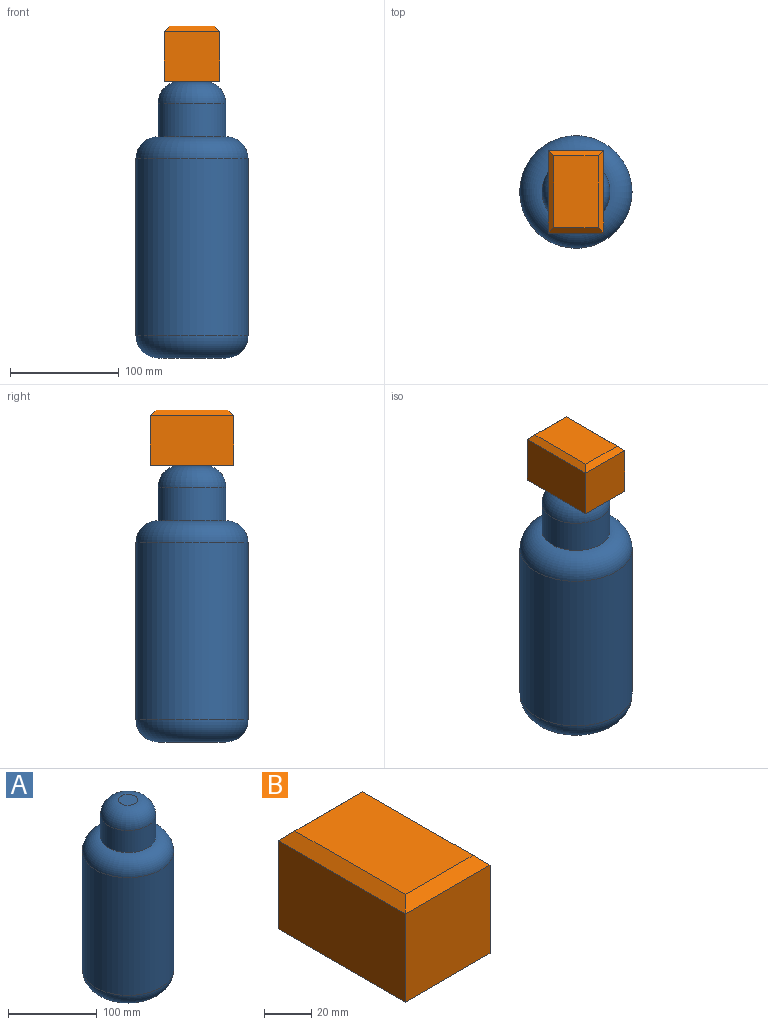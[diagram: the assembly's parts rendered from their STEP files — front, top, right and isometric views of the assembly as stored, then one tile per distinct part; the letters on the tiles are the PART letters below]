
ASSEMBLY  parts=2 mates=1
PART A: 7 faces, bbox 111.5x111.5x254 mm
  f0: cylinder r=51.5mm len=162.56mm, axis (0,0,-1), area 52597mm2, adj f2,f3
  f1: plane 62.35x62.35mm, normal (0,0,-1), area 3053.3mm2, adj f2
  f2: torus R=31.18mm, axis (0,0,1), area 8846.6mm2, adj f0,f1
  f3: torus R=31.18mm, axis (0,0,1), area 8846.6mm2, adj f0,f4
  f4: cylinder r=31.18mm len=62.35mm, axis (0,0,-1), area 5970.4mm2, adj f3,f6
  f5: plane 21.71x21.71mm, normal (0,0,1), area 370.2mm2, adj f6
  f6: torus R=10.86mm, axis (0,0,1), area 4771.4mm2, adj f4,f5
PART B: 10 faces, bbox 50.8x76.2x50.8 mm
  f0: plane 76.2x45.72mm, normal (1,0,0), area 3483.9mm2, adj f1,f3,f5,f7
  f1: plane 50.8x45.72mm, normal (0,1,0), area 2322.6mm2, adj f0,f2,f5,f9
  f2: plane 76.2x45.72mm, normal (-1,0,0), area 3483.9mm2, adj f1,f3,f5,f8
  f3: plane 50.8x45.72mm, normal (0,-1,0), area 2322.6mm2, adj f0,f2,f5,f6
  f4: plane 66.04x40.64mm, normal (0,0,1), area 2683.9mm2, adj f6,f7,f8,f9
  f5: plane 76.2x50.8mm, normal (0,0,-1), area 3871mm2, adj f0,f1,f2,f3
  f6: plane 50.8x5.08mm, normal (0,-0.71,0.71), area 328.5mm2, adj f3,f4,f7,f8
  f7: plane 76.2x5.08mm, normal (0.71,0,0.71), area 510.9mm2, adj f0,f4,f6,f9
  f8: plane 76.2x5.08mm, normal (-0.71,0,0.71), area 510.9mm2, adj f2,f4,f6,f9
  f9: plane 50.8x5.08mm, normal (0,0.71,0.71), area 328.5mm2, adj f1,f4,f7,f8
PLACE A t=(-114.62,12.78,-8.57)mm fixed
PLACE B t=(-114.62,12.78,245.43)mm
MATE planar B.f5 <-> A.f0  axis (0,0,-1) through (-114.62,12.78,245.43)mm
